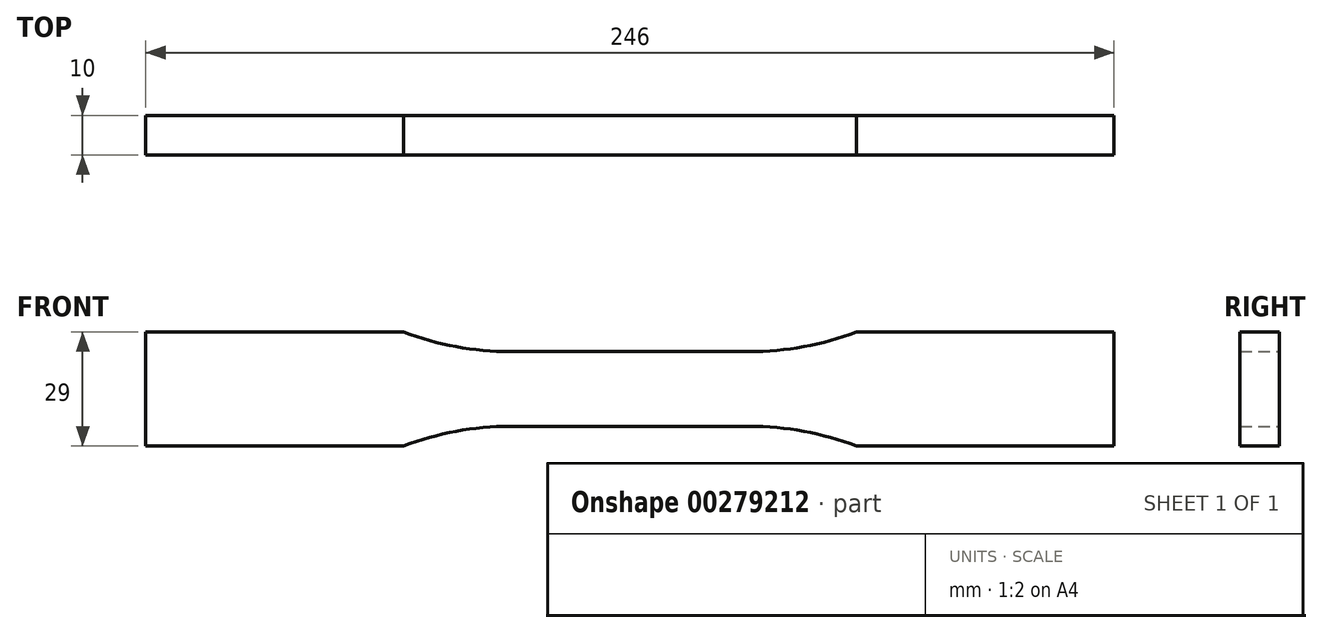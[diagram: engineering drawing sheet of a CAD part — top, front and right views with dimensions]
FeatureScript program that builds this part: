
annotation { "Feature Type Name" : "Feature", "Feature Type Description" : "" }
export const myFeature = defineFeature(function(context is Context, id is Id, definition is map)
    precondition{}
    {
        {
            var Q0;
            Q0=qCreatedBy(makeId("Front.planeOp"),FACE);
            var sketch = newSketch(context, id + "F0", { "sketchPlane" : qUnion([Q0])});
            skLineSegment(sketch, "E0", {"start": v(0, 9.5) * mm, "end": v(30.39, 9.5) * mm});
            skArc(sketch, "E1", {"start": v(30.39, 9.5) * mm, "mid": v(44.17, 10.76) * mm, "end": v(57.5, 14.5) * mm});
            skLineSegment(sketch, "E2", {"start": v(57.5, 14.5) * mm, "end": v(123, 14.5) * mm});
            skLineSegment(sketch, "E3.MirrorCS", {"start": v(0, -9.5) * mm, "end": v(30.39, -9.5) * mm});
            skLineSegment(sketch, "E4.MirrorCS", {"start": v(57.5, -14.5) * mm, "end": v(123, -14.5) * mm});
            skArc(sketch, "E5.MirrorCS", {"start": v(30.39, -9.5) * mm, "mid": v(44.17, -10.76) * mm, "end": v(57.5, -14.5) * mm});
            skLineSegment(sketch, "E6.MirrorCS", {"start": v(-57.5, 14.5) * mm, "end": v(-123, 14.5) * mm});
            skLineSegment(sketch, "E7.MirrorCS", {"start": v(-57.5, -14.5) * mm, "end": v(-123, -14.5) * mm});
            skArc(sketch, "E8.MirrorCS", {"start": v(-30.39, -9.5) * mm, "mid": v(-44.17, -10.76) * mm, "end": v(-57.5, -14.5) * mm});
            skLineSegment(sketch, "E9.MirrorCS", {"start": v(0, 9.5) * mm, "end": v(-30.39, 9.5) * mm});
            skArc(sketch, "E10.MirrorCS", {"start": v(-30.39, 9.5) * mm, "mid": v(-44.17, 10.76) * mm, "end": v(-57.5, 14.5) * mm});
            skLineSegment(sketch, "E11.MirrorCS", {"start": v(0, -9.5) * mm, "end": v(-30.39, -9.5) * mm});
            skLineSegment(sketch, "E12", {"start": v(-123, -14.5) * mm, "end": v(-123, 14.5) * mm});
            skLineSegment(sketch, "E13", {"start": v(123, -14.5) * mm, "end": v(123, 14.5) * mm});
            skSolve(sketch);
        }
        {
            var Q0;
            Q0 = qSketchRegion(id + "F0", true);
            extrude(context, id + "F1", {"entities" : qUnion([Q0]), "endBound" : BoundingType.SYMMETRIC, "depth" : 10 * mm});
        }
    });
